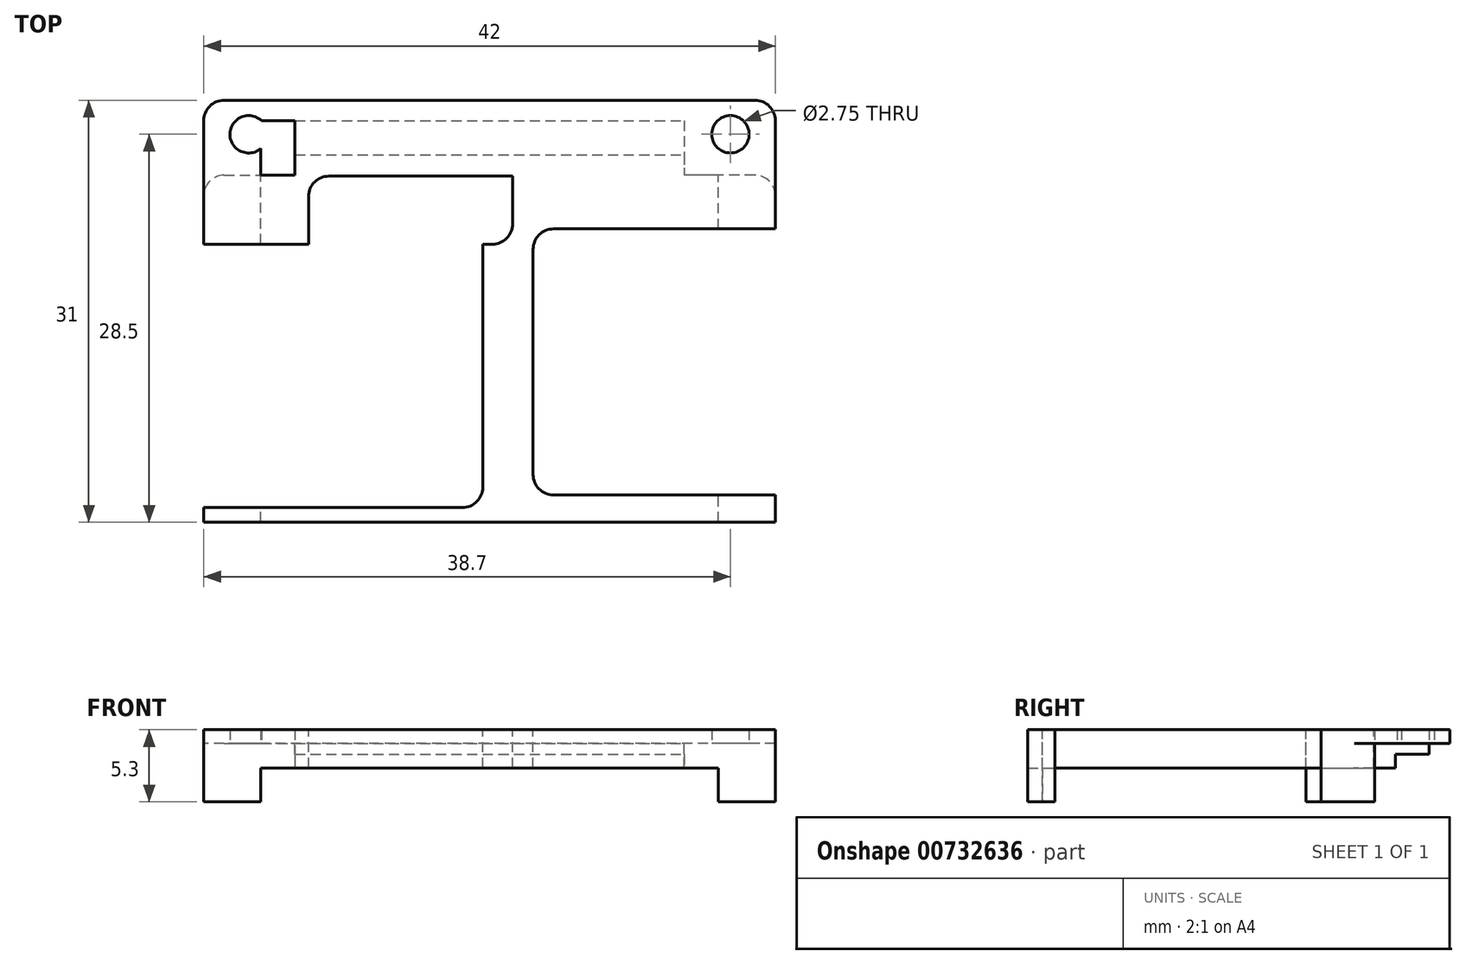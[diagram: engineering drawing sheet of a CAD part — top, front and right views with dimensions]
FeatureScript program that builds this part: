
annotation { "Feature Type Name" : "Feature", "Feature Type Description" : "" }
export const myFeature = defineFeature(function(context is Context, id is Id, definition is map)
    precondition{}
    {
        {
            var Q0;
            Q0=qCreatedBy(makeId("Top.planeOp"),FACE);
            var sketch = newSketch(context, id + "F0", { "sketchPlane" : qUnion([Q0])});
            skLineSegment(sketch, "E0.bottom", {"start": v(21, -16) * mm, "end": v(-21, -16) * mm});
            skLineSegment(sketch, "E0.top", {"start": v(21, 16) * mm, "end": v(-21, 16) * mm});
            skLineSegment(sketch, "E0.left", {"start": v(21, -16) * mm, "end": v(21, 16) * mm});
            skLineSegment(sketch, "E0.right", {"start": v(-21, -16) * mm, "end": v(-21, 16) * mm});
            skPoint(sketch, "E0.middle", {"position": v(0, 0) * mm});
            skCircle(sketch, "E1", {"center": v(-17.7, 13.5) * mm, "radius": 1.38 * mm});
            skCircle(sketch, "E2.MirrorC", {"center": v(17.7, 13.5) * mm, "radius": 1.38 * mm});
            skLineSegment(sketch, "E3.bottom", {"start": v(-16.8, -16) * mm, "end": v(16.8, -16) * mm});
            skLineSegment(sketch, "E3.top", {"start": v(-16.8, 14.5) * mm, "end": v(16.8, 14.5) * mm});
            skLineSegment(sketch, "E3.left", {"start": v(-16.8, -16) * mm, "end": v(-16.8, 14.5) * mm});
            skLineSegment(sketch, "E3.right", {"start": v(16.8, -16) * mm, "end": v(16.8, 14.5) * mm});
            skPoint(sketch, "E4", {"position": v(0, 14.5) * mm});
            skLineSegment(sketch, "E5.bottom", {"start": v(-21, 16) * mm, "end": v(-16.8, 16) * mm});
            skLineSegment(sketch, "E5.top", {"start": v(-21, 10.5) * mm, "end": v(-16.8, 10.5) * mm});
            skLineSegment(sketch, "E5.left", {"start": v(-21, 16) * mm, "end": v(-21, 10.5) * mm});
            skLineSegment(sketch, "E5.right", {"start": v(-16.8, 16) * mm, "end": v(-16.8, 10.5) * mm});
            skLineSegment(sketch, "E6.MirrorCS", {"start": v(16.8, 16) * mm, "end": v(16.8, 10.5) * mm});
            skLineSegment(sketch, "E7.MirrorCS", {"start": v(21, 10.5) * mm, "end": v(16.8, 10.5) * mm});
            skLineSegment(sketch, "E8", {"start": v(-11.95, 16) * mm, "end": v(-11.95, 14.5) * mm});
            skLineSegment(sketch, "E9.MirrorCS", {"start": v(11.95, 16) * mm, "end": v(11.95, 14.5) * mm});
            skLineSegment(sketch, "E10.bottom", {"start": v(-16.8, 14.5) * mm, "end": v(-14.3, 14.5) * mm});
            skLineSegment(sketch, "E10.top", {"start": v(-16.8, 10.5) * mm, "end": v(-14.3, 10.5) * mm});
            skLineSegment(sketch, "E10.left", {"start": v(-16.8, 14.5) * mm, "end": v(-16.8, 10.5) * mm});
            skLineSegment(sketch, "E10.right", {"start": v(-14.3, 14.5) * mm, "end": v(-14.3, 10.5) * mm});
            skLineSegment(sketch, "E11.MirrorCS", {"start": v(14.3, 14.5) * mm, "end": v(14.3, 10.5) * mm});
            skLineSegment(sketch, "E12.MirrorCS", {"start": v(16.8, 10.5) * mm, "end": v(14.3, 10.5) * mm});
            skSolve(sketch);
        }
        {
            var Q0;
            {var subQ8=sQuery(id+"F0.wireOp",EDGE,"E5.top");Q0=makeQuery(id+"F0.imprint","IMPRINT",FACE,{"disambiguationData":[TD([[makeQuery(id+"F0.imprint","IMPRINT",EDGE,{"derivedFrom":subQ8}),1.0]])]});}
            var Q1;
            {var subQ5=sQuery(id+"F0.wireOp",EDGE,"E8");Q1=makeQuery(id+"F0.imprint","IMPRINT",FACE,{"disambiguationData":[TD([[makeQuery(id+"F0.imprint","IMPRINT",EDGE,{"derivedFrom":subQ5}),-1.0]])]});}
            var Q2;
            {var subQ2=sQuery(id+"F0.wireOp",EDGE,"E8");Q2=makeQuery(id+"F0.imprint","IMPRINT",FACE,{"disambiguationData":[TD([[makeQuery(id+"F0.imprint","IMPRINT",EDGE,{"derivedFrom":subQ2}),1.0]])]});}
            var Q3;
            {var subQ5=sQuery(id+"F0.wireOp",EDGE,"E9.MirrorCS");Q3=makeQuery(id+"F0.imprint","IMPRINT",FACE,{"disambiguationData":[TD([[makeQuery(id+"F0.imprint","IMPRINT",EDGE,{"derivedFrom":subQ5}),1.0]])]});}
            var Q4;
            {var subQ3=sQuery(id+"F0.wireOp",EDGE,"E7.MirrorCS");Q4=makeQuery(id+"F0.imprint","IMPRINT",FACE,{"disambiguationData":[TD([[makeQuery(id+"F0.imprint","IMPRINT",EDGE,{"derivedFrom":subQ3}),-1.0]])]});}
            var Q5;
            {var subQ6=sQuery(id+"F0.wireOp",EDGE,"E1");var subQ15=makeQuery(id+"F0.imprint","IMPRINT",VERTEX,{"derivedFrom":subQ6});Q5=makeQuery(id+"F0.imprint","IMPRINT",FACE,{"disambiguationData":[TD([[makeQuery(id+"F0.imprint","IMPRINT",EDGE,{"disambiguationData":[TD([[subQ15,-1.0]])],"derivedFrom":subQ6}),-1.0]])]});}
            var Q6;
            {var subQ5=sQuery(id+"F0.wireOp",EDGE,"E7.MirrorCS");Q6=makeQuery(id+"F0.imprint","IMPRINT",FACE,{"disambiguationData":[TD([[makeQuery(id+"F0.imprint","IMPRINT",EDGE,{"derivedFrom":subQ5}),1.0]])]});}
            var Q7;
            {var subQ5=sQuery(id+"F0.wireOp",EDGE,"E5.top");Q7=makeQuery(id+"F0.imprint","IMPRINT",FACE,{"disambiguationData":[TD([[makeQuery(id+"F0.imprint","IMPRINT",EDGE,{"derivedFrom":subQ5}),-1.0]])]});}
            var Q8;
            {var subQ4=sQuery(id+"F0.wireOp",EDGE,"E11.MirrorCS");Q8=makeQuery(id+"F0.imprint","IMPRINT",FACE,{"disambiguationData":[TD([[makeQuery(id+"F0.imprint","IMPRINT",EDGE,{"derivedFrom":subQ4}),1.0]])]});}
            var Q9;
            {var subQ11=sQuery(id+"F0.wireOp",EDGE,"E10.top");Q9=makeQuery(id+"F0.imprint","IMPRINT",FACE,{"disambiguationData":[TD([[makeQuery(id+"F0.imprint","IMPRINT",EDGE,{"derivedFrom":subQ11}),-1.0]])]});}
            extrude(context, id + "F1", {"entities" : qUnion([Q0, Q1, Q2, Q3, Q4, Q5, Q6, Q7, Q8, Q9]), "depth" : 1 * mm, "offsetDistance" : 25 * mm});
        }
        {
            var Q0;
            {var subQ5=sQuery(id+"F0.wireOp",EDGE,"E7.MirrorCS");Q0=makeQuery(id+"F0.imprint","IMPRINT",FACE,{"disambiguationData":[TD([[makeQuery(id+"F0.imprint","IMPRINT",EDGE,{"derivedFrom":subQ5}),1.0]])]});}
            var Q1;
            {var subQ1=sQuery(id+"F0.wireOp",EDGE,"E3.top");Q1=makeQuery(id+"F0.imprint","IMPRINT",FACE,{"disambiguationData":[TD([[makeQuery(id+"F0.imprint","IMPRINT",EDGE,{"derivedFrom":subQ1}),-1.0]])]});}
            var Q2;
            {var subQ5=sQuery(id+"F0.wireOp",EDGE,"E5.top");Q2=makeQuery(id+"F0.imprint","IMPRINT",FACE,{"disambiguationData":[TD([[makeQuery(id+"F0.imprint","IMPRINT",EDGE,{"derivedFrom":subQ5}),-1.0]])]});}
            extrude(context, id + "F2", {"entities" : qUnion([Q0, Q1, Q2]), "operationType" : NewBodyOperationType.ADD, "oppositeDirection" : true, "depth" : 1.8 * mm, "offsetDistance" : 25 * mm});
        }
        {
            var Q0;
            {var subQ5=sQuery(id+"F0.wireOp",EDGE,"E5.top");Q0=makeQuery(id+"F0.imprint","IMPRINT",FACE,{"disambiguationData":[TD([[makeQuery(id+"F0.imprint","IMPRINT",EDGE,{"derivedFrom":subQ5}),-1.0]])]});}
            var Q1;
            {var subQ5=sQuery(id+"F0.wireOp",EDGE,"E7.MirrorCS");Q1=makeQuery(id+"F0.imprint","IMPRINT",FACE,{"disambiguationData":[TD([[makeQuery(id+"F0.imprint","IMPRINT",EDGE,{"derivedFrom":subQ5}),1.0]])]});}
            extrude(context, id + "F3", {"entities" : qUnion([Q0, Q1]), "operationType" : NewBodyOperationType.ADD, "oppositeDirection" : true, "depth" : 4.3 * mm, "offsetDistance" : 25 * mm});
        }
        {
            var Q0;
            Q0=makeQuery(id+"F1.opExtrude","CAP_FACE",FACE,{"disambiguationData":[OSD([sQuery(id+"F0.wireOp",EDGE,"E0.bottom"),sQuery(id+"F0.wireOp",EDGE,"E0.top"),sQuery(id+"F0.wireOp",EDGE,"E0.left"),sQuery(id+"F0.wireOp",EDGE,"E0.right"),sQuery(id+"F0.wireOp",EDGE,"E1"),sQuery(id+"F0.wireOp",EDGE,"E2.MirrorC")])],"isStart":false});
            var sketch = newSketch(context, id + "F4", { "sketchPlane" : qUnion([Q0])});
            skLineSegment(sketch, "E13.bottom", {"start": v(-21, -13.93) * mm, "end": v(-0.5, -13.93) * mm});
            skLineSegment(sketch, "E13.top", {"start": v(-21, 5.43) * mm, "end": v(-0.5, 5.43) * mm});
            skLineSegment(sketch, "E13.left", {"start": v(-21, -13.93) * mm, "end": v(-21, 5.43) * mm});
            skLineSegment(sketch, "E13.right", {"start": v(-0.5, -13.93) * mm, "end": v(-0.5, 5.43) * mm});
            skLineSegment(sketch, "E14.bottom", {"start": v(21, -13) * mm, "end": v(3.2, -13) * mm});
            skLineSegment(sketch, "E14.top", {"start": v(21, 6.55) * mm, "end": v(3.2, 6.55) * mm});
            skLineSegment(sketch, "E14.left", {"start": v(21, -13) * mm, "end": v(21, 6.55) * mm});
            skLineSegment(sketch, "E14.right", {"start": v(3.2, -13) * mm, "end": v(3.2, 6.55) * mm});
            skLineSegment(sketch, "E15.bottom", {"start": v(21, 16) * mm, "end": v(-21, 16) * mm});
            skLineSegment(sketch, "E15.top", {"start": v(21, 12) * mm, "end": v(-21, 12) * mm});
            skLineSegment(sketch, "E15.left", {"start": v(21, 16) * mm, "end": v(21, 12) * mm});
            skLineSegment(sketch, "E15.right", {"start": v(-21, 16) * mm, "end": v(-21, 12) * mm});
            skPoint(sketch, "E15.middle", {"position": v(0, 14) * mm});
            skLineSegment(sketch, "E16.bottom", {"start": v(1.7, 5.43) * mm, "end": v(-13.3, 5.43) * mm});
            skLineSegment(sketch, "E16.top", {"start": v(1.7, 10.43) * mm, "end": v(-13.3, 10.43) * mm});
            skLineSegment(sketch, "E16.left", {"start": v(1.7, 5.43) * mm, "end": v(1.7, 10.43) * mm});
            skLineSegment(sketch, "E16.right", {"start": v(-13.3, 5.43) * mm, "end": v(-13.3, 10.43) * mm});
            skLineSegment(sketch, "E17", {"start": v(21, -15) * mm, "end": v(-21, -15) * mm});
            skLineSegment(sketch, "E18", {"start": v(-15.13, 12) * mm, "end": v(-15.13, 16) * mm});
            skLineSegment(sketch, "E19.MirrorCS", {"start": v(15.13, 12) * mm, "end": v(15.13, 16) * mm});
            skSolve(sketch);
        }
        {
            var Q0;
            Q0=makeQuery(id+"F4.imprint","IMPRINT",FACE,{"disambiguationData":[TD([[makeQuery(id+"F4.imprint","IMPRINT",EDGE,{"derivedFrom":sQuery(id+"F4.wireOp",EDGE,"E13.bottom")}),1.0]])]});
            var Q1;
            Q1=makeQuery(id+"F4.imprint","IMPRINT",FACE,{"disambiguationData":[TD([[makeQuery(id+"F4.imprint","IMPRINT",EDGE,{"derivedFrom":sQuery(id+"F4.wireOp",EDGE,"E14.bottom")}),-1.0]])]});
            var Q2;
            {var subQ0=sQuery(id+"F4.wireOp",EDGE,"E18");Q2=makeQuery(id+"F4.imprint","IMPRINT",FACE,{"disambiguationData":[TD([[makeQuery(id+"F4.imprint","IMPRINT",EDGE,{"derivedFrom":subQ0}),-1.0]])]});}
            var Q3;
            Q3=makeQuery(id+"F4.imprint","IMPRINT",FACE,{"disambiguationData":[TD([[makeQuery(id+"F4.imprint","IMPRINT",EDGE,{"derivedFrom":sQuery(id+"F4.wireOp",EDGE,"E16.top")}),1.0]])]});
            var Q4;
            {var subQ0=sQuery(id+"F4.wireOp",EDGE,"E17");Q4=makeQuery(id+"F4.imprint","IMPRINT",FACE,{"disambiguationData":[TD([[makeQuery(id+"F4.imprint","IMPRINT",EDGE,{"derivedFrom":subQ0}),1.0]])]});}
            extrude(context, id + "F5", {"entities" : qUnion([Q0, Q1, Q2, Q3, Q4]), "operationType" : NewBodyOperationType.REMOVE, "endBound" : BoundingType.THROUGH_ALL, "oppositeDirection" : true, "depth" : 25 * mm, "offsetDistance" : 25 * mm});
        }
        {
            var Q0;
            Q0=makeQuery(id+"F2.opExtrude","CAP_FACE",FACE,{"disambiguationData":[OSD([sQuery(id+"F0.wireOp",EDGE,"E0.bottom"),sQuery(id+"F0.wireOp",EDGE,"E0.left"),sQuery(id+"F0.wireOp",EDGE,"E0.right"),sQuery(id+"F0.wireOp",EDGE,"E3.top"),sQuery(id+"F0.wireOp",EDGE,"E5.top"),sQuery(id+"F0.wireOp",EDGE,"E7.MirrorCS"),sQuery(id+"F0.wireOp",EDGE,"E10.top"),sQuery(id+"F0.wireOp",EDGE,"E10.right"),sQuery(id+"F0.wireOp",EDGE,"E11.MirrorCS"),sQuery(id+"F0.wireOp",EDGE,"E12.MirrorCS")])],"isStart":false});
            var sketch = newSketch(context, id + "F6", { "sketchPlane" : qUnion([Q0])});
            skLineSegment(sketch, "E20.bottom", {"start": v(-14.3, -5.43) * mm, "end": v(14.3, -5.43) * mm});
            skLineSegment(sketch, "E20.top", {"start": v(-14.3, -12) * mm, "end": v(14.3, -12) * mm});
            skLineSegment(sketch, "E20.left", {"start": v(-14.3, -5.43) * mm, "end": v(-14.3, -12) * mm});
            skLineSegment(sketch, "E20.right", {"start": v(14.3, -5.43) * mm, "end": v(14.3, -12) * mm});
            skSolve(sketch);
        }
        {
            var Q0;
            {var subQ14=sQuery(id+"F6.wireOp",EDGE,"E20.top");Q0=makeQuery(id+"F6.imprint","IMPRINT",FACE,{"disambiguationData":[TD([[makeQuery(id+"F6.imprint","IMPRINT",EDGE,{"derivedFrom":subQ14}),-1.0]])]});}
            extrude(context, id + "F7", {"entities" : qUnion([Q0]), "operationType" : NewBodyOperationType.REMOVE, "oppositeDirection" : true, "depth" : 1 * mm, "offsetDistance" : 25 * mm});
        }
        {
            var Q0;
            Q0=makeQuery(id+"F1.opExtrude","SWEPT_EDGE",EDGE,{"disambiguationData":[OSD([sQuery(id+"F0.wireOp",EDGE,"E0.top"),sQuery(id+"F0.wireOp",EDGE,"E0.right")])]});
            var Q1;
            Q1=makeQuery(id+"F1.opExtrude","SWEPT_EDGE",EDGE,{"disambiguationData":[OSD([sQuery(id+"F0.wireOp",EDGE,"E0.top"),sQuery(id+"F0.wireOp",EDGE,"E0.left")])]});
            var Q2;
            Q2=makeQuery(id+"F2.opExtrude","SWEPT_EDGE",EDGE,{"disambiguationData":[OSD([sQuery(id+"F0.wireOp",EDGE,"E3.right"),sQuery(id+"F0.wireOp",EDGE,"E7.MirrorCS")])]});
            var Q3;
            Q3=makeQuery(id+"F2.opExtrude","SWEPT_EDGE",EDGE,{"disambiguationData":[OSD([sQuery(id+"F0.wireOp",EDGE,"E3.left"),sQuery(id+"F0.wireOp",EDGE,"E5.top")])]});
            var Q4;
            Q4=makeQuery(id+"F5.boolean.opBoolean","COPY",EDGE,{"derivedFrom":makeQuery(id+"F5.opExtrude","SWEPT_EDGE",EDGE,{"disambiguationData":[OSD([sQuery(id+"F0.wireOp",EDGE,"E0.right"),sQuery(id+"F4.wireOp",EDGE,"E13.top"),sQuery(id+"F4.wireOp",EDGE,"E13.left")])]})});
            var Q5;
            Q5=makeQuery(id+"F5.boolean.opBoolean","COPY",EDGE,{"derivedFrom":makeQuery(id+"F5.opExtrude","SWEPT_EDGE",EDGE,{"disambiguationData":[OSD([sQuery(id+"F0.wireOp",EDGE,"E0.left"),sQuery(id+"F4.wireOp",EDGE,"E14.top"),sQuery(id+"F4.wireOp",EDGE,"E14.left")])]})});
            var Q6;
            {var subQ0=sQuery(id+"F0.wireOp",EDGE,"E0.left");var subQ1=sQuery(id+"F0.wireOp",EDGE,"E0.bottom");Q6=makeQuery(id+"F3.boolean.opBoolean","MERGE",EDGE,{"derivedFrom":[makeQuery(id+"F2.boolean.opBoolean","MERGE",EDGE,{"derivedFrom":[makeQuery(id+"F1.opExtrude","SWEPT_EDGE",EDGE,{"disambiguationData":[OSD([subQ1,subQ0])]}),makeQuery(id+"F2.opExtrude","SWEPT_EDGE",EDGE,{"disambiguationData":[OSD([subQ1,subQ0])]})]}),makeQuery(id+"F3.opExtrude","SWEPT_EDGE",EDGE,{"disambiguationData":[OSD([subQ1,subQ0])]})]});}
            var Q7;
            {var subQ0=sQuery(id+"F0.wireOp",EDGE,"E0.right");var subQ1=sQuery(id+"F0.wireOp",EDGE,"E0.bottom");Q7=makeQuery(id+"F3.boolean.opBoolean","MERGE",EDGE,{"derivedFrom":[makeQuery(id+"F2.boolean.opBoolean","MERGE",EDGE,{"derivedFrom":[makeQuery(id+"F1.opExtrude","SWEPT_EDGE",EDGE,{"disambiguationData":[OSD([subQ1,subQ0])]}),makeQuery(id+"F2.opExtrude","SWEPT_EDGE",EDGE,{"disambiguationData":[OSD([subQ1,subQ0])]})]}),makeQuery(id+"F3.opExtrude","SWEPT_EDGE",EDGE,{"disambiguationData":[OSD([subQ1,subQ0])]})]});}
            var Q8;
            Q8=makeQuery(id+"F5.boolean.opBoolean","COPY",EDGE,{"derivedFrom":makeQuery(id+"F5.opExtrude","SWEPT_EDGE",EDGE,{"disambiguationData":[OSD([sQuery(id+"F4.wireOp",EDGE,"E15.bottom"),sQuery(id+"F4.wireOp",EDGE,"E18")])]})});
            var Q9;
            Q9=makeQuery(id+"F5.boolean.opBoolean","COPY",EDGE,{"derivedFrom":makeQuery(id+"F5.opExtrude","SWEPT_EDGE",EDGE,{"disambiguationData":[OSD([sQuery(id+"F4.wireOp",EDGE,"E15.bottom"),sQuery(id+"F4.wireOp",EDGE,"E19.MirrorCS")])]})});
            var Q10;
            Q10=makeQuery(id+"F5.boolean.opBoolean","COPY",EDGE,{"derivedFrom":makeQuery(id+"F5.opExtrude","SWEPT_EDGE",EDGE,{"disambiguationData":[OSD([sQuery(id+"F4.wireOp",EDGE,"E15.top"),sQuery(id+"F4.wireOp",EDGE,"E19.MirrorCS")])]})});
            var Q11;
            Q11=makeQuery(id+"F5.boolean.opBoolean","COPY",EDGE,{"derivedFrom":makeQuery(id+"F5.opExtrude","SWEPT_EDGE",EDGE,{"disambiguationData":[OSD([sQuery(id+"F4.wireOp",EDGE,"E15.top"),sQuery(id+"F4.wireOp",EDGE,"E18")])]})});
            var Q12;
            Q12=makeQuery(id+"F5.boolean.opBoolean","COPY",EDGE,{"derivedFrom":makeQuery(id+"F5.opExtrude","SWEPT_EDGE",EDGE,{"disambiguationData":[OSD([sQuery(id+"F4.wireOp",EDGE,"E15.top"),sQuery(id+"F4.wireOp",EDGE,"E19.MirrorCS")])]})});
            var Q13;
            Q13=makeQuery(id+"F5.boolean.opBoolean","COPY",EDGE,{"derivedFrom":makeQuery(id+"F5.opExtrude","SWEPT_EDGE",EDGE,{"disambiguationData":[OSD([sQuery(id+"F4.wireOp",EDGE,"E15.top"),sQuery(id+"F4.wireOp",EDGE,"E18")])]})});
            var Q14;
            Q14=makeQuery(id+"F5.boolean.opBoolean","COPY",EDGE,{"derivedFrom":makeQuery(id+"F5.opExtrude","SWEPT_EDGE",EDGE,{"disambiguationData":[OSD([sQuery(id+"F4.wireOp",EDGE,"E14.top"),sQuery(id+"F4.wireOp",EDGE,"E14.right")])]})});
            var Q15;
            Q15=makeQuery(id+"F5.boolean.opBoolean","COPY",EDGE,{"derivedFrom":makeQuery(id+"F5.opExtrude","SWEPT_EDGE",EDGE,{"disambiguationData":[OSD([sQuery(id+"F4.wireOp",EDGE,"E14.bottom"),sQuery(id+"F4.wireOp",EDGE,"E14.right")])]})});
            var Q16;
            Q16=makeQuery(id+"F5.boolean.opBoolean","COPY",EDGE,{"derivedFrom":makeQuery(id+"F5.opExtrude","SWEPT_EDGE",EDGE,{"disambiguationData":[OSD([sQuery(id+"F4.wireOp",EDGE,"E13.bottom"),sQuery(id+"F4.wireOp",EDGE,"E13.right")])]})});
            var Q17;
            Q17=makeQuery(id+"F5.boolean.opBoolean","COPY",EDGE,{"derivedFrom":makeQuery(id+"F5.opExtrude","SWEPT_EDGE",EDGE,{"disambiguationData":[OSD([sQuery(id+"F4.wireOp",EDGE,"E16.top"),sQuery(id+"F4.wireOp",EDGE,"E16.right")])]})});
            var Q18;
            Q18=makeQuery(id+"F5.boolean.opBoolean","COPY",EDGE,{"derivedFrom":makeQuery(id+"F5.opExtrude","SWEPT_EDGE",EDGE,{"disambiguationData":[OSD([sQuery(id+"F4.wireOp",EDGE,"E16.bottom"),sQuery(id+"F4.wireOp",EDGE,"E16.left")])]})});
            fillet(context, id + "F8", {"entities" : qUnion([Q0, Q1, Q2, Q3, Q4, Q5, Q6, Q7, Q8, Q9, Q10, Q11, Q12, Q13, Q14, Q15, Q16, Q17, Q18]), "tangentPropagation" : true, "radius" : 1.5 * mm, "defaultsChanged" : false, "vertexSettings" : [], "allowEdgeOverflow" : false});
        }
    });
